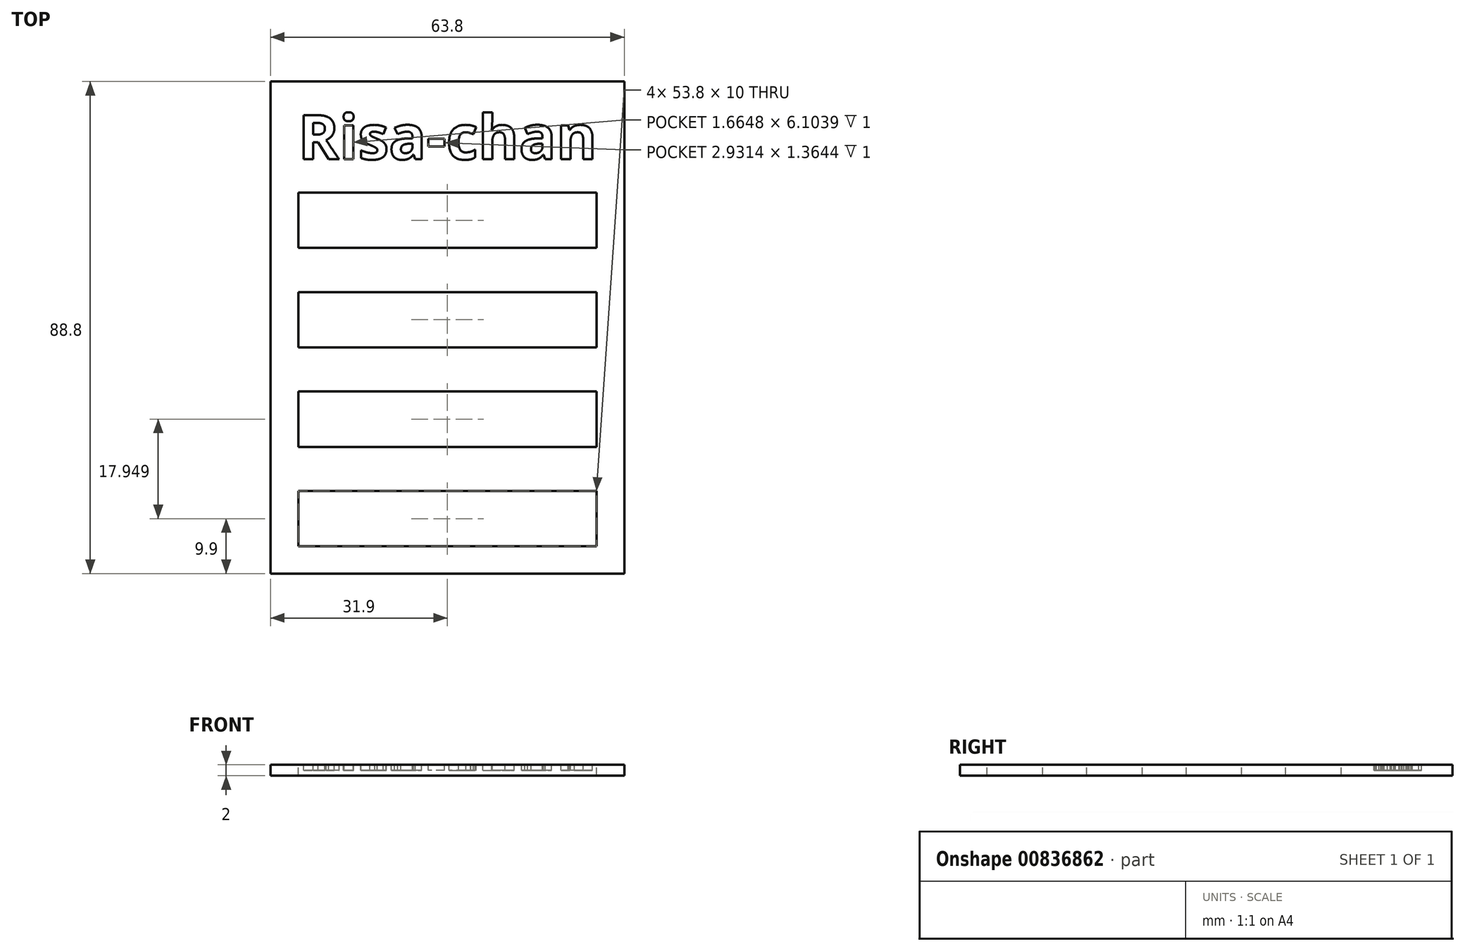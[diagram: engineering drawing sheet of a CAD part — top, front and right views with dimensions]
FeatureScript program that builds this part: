
annotation { "Feature Type Name" : "Feature", "Feature Type Description" : "" }
export const myFeature = defineFeature(function(context is Context, id is Id, definition is map)
    precondition{}
    {
        {
            var Q0;
            Q0=qCreatedBy(makeId("Top.planeOp"),FACE);
            var sketch = newSketch(context, id + "F0", { "sketchPlane" : qUnion([Q0])});
            skLineSegment(sketch, "E0.bottom", {"start": v(32, -44.5) * mm, "end": v(-32, -44.5) * mm});
            skLineSegment(sketch, "E0.top", {"start": v(32, 44.5) * mm, "end": v(-32, 44.5) * mm});
            skLineSegment(sketch, "E0.left", {"start": v(32, -44.5) * mm, "end": v(32, 44.5) * mm});
            skLineSegment(sketch, "E0.right", {"start": v(-32, -44.5) * mm, "end": v(-32, 44.5) * mm});
            skLineSegment(sketch, "E1.0", {"start": v(31.9, 44.4) * mm, "end": v(-31.9, 44.4) * mm});
            skLineSegment(sketch, "E1.1", {"start": v(31.9, -44.4) * mm, "end": v(31.9, 44.4) * mm});
            skLineSegment(sketch, "E1.2", {"start": v(31.9, -44.4) * mm, "end": v(-31.9, -44.4) * mm});
            skLineSegment(sketch, "E1.3", {"start": v(-31.9, -44.4) * mm, "end": v(-31.9, 44.4) * mm});
            skSolve(sketch);
        }
        {
            var Q0;
            Q0=makeQuery(id+"F0.imprint","IMPRINT",FACE,{"disambiguationData":[TD([[makeQuery(id+"F0.imprint","IMPRINT",EDGE,{"derivedFrom":sQuery(id+"F0.wireOp",EDGE,"E1.0")}),1.0]])]});
            extrude(context, id + "F1", {"entities" : qUnion([Q0]), "depth" : 2 * mm, "offsetDistance" : 25 * mm});
        }
        {
            var Q0;
            Q0=makeQuery(id+"F1.opExtrude","CAP_FACE",FACE,{"disambiguationData":[OSD([sQuery(id+"F0.wireOp",EDGE,"E1.0"),sQuery(id+"F0.wireOp",EDGE,"E1.1"),sQuery(id+"F0.wireOp",EDGE,"E1.2"),sQuery(id+"F0.wireOp",EDGE,"E1.3")])],"isStart":false});
            var sketch = newSketch(context, id + "F2", { "sketchPlane" : qUnion([Q0])});
            skText(sketch, "E2", { "text": "Risa-chan", "fontName": "OpenSans-Bold.ttf"});
            const initialGuessF2  = {"E2": [-0.0269, 0.03035, 1, 0, 0.00805]};
            skSetInitialGuess(sketch, initialGuessF2);
            skSolve(sketch);
        }
        {
            var Q0;
            Q0=qSketchRegion(id+"F2",true);
            extrude(context, id + "F3", {"entities" : qUnion([Q0]), "operationType" : NewBodyOperationType.REMOVE, "oppositeDirection" : true, "depth" : 1 * mm, "offsetDistance" : 25 * mm});
        }
        {
            var Q0;
            {var subQ0=sQuery(id+"F0.wireOp",EDGE,"E1.1");var subQ1=sQuery(id+"F0.wireOp",EDGE,"E1.3");var subQ2=sQuery(id+"F0.wireOp",EDGE,"E1.0");var subQ3=sQuery(id+"F0.wireOp",EDGE,"E1.2");Q0=makeQuery(id+"F3.boolean.opBoolean","SPLIT",FACE,{"disambiguationData":[TD([makeQuery(id+"F1.opExtrude","SWEPT_FACE",FACE,{"disambiguationData":[OSD([subQ2])]})])],"derivedFrom":makeQuery(id+"F1.opExtrude","CAP_FACE",FACE,{"disambiguationData":[OSD([subQ2,subQ0,subQ3,subQ1])],"isStart":false})});}
            var sketch = newSketch(context, id + "F4", { "sketchPlane" : qUnion([Q0])});
            skLineSegment(sketch, "E3.bottom", {"start": v(-26.9, 24.35) * mm, "end": v(26.9, 24.35) * mm});
            skLineSegment(sketch, "E3.top", {"start": v(-26.9, 14.35) * mm, "end": v(26.9, 14.35) * mm});
            skLineSegment(sketch, "E3.left", {"start": v(-26.9, 24.35) * mm, "end": v(-26.9, 14.35) * mm});
            skLineSegment(sketch, "E3.right", {"start": v(26.9, 24.35) * mm, "end": v(26.9, 14.35) * mm});
            skLineSegment(sketch, "E4.0.1.0", {"start": v(-26.9, -3.6) * mm, "end": v(26.9, -3.6) * mm});
            skLineSegment(sketch, "E4.0.1.1", {"start": v(26.9, 6.4) * mm, "end": v(26.9, -3.6) * mm});
            skLineSegment(sketch, "E4.0.1.2", {"start": v(-26.9, 6.4) * mm, "end": v(-26.9, -3.6) * mm});
            skLineSegment(sketch, "E4.0.1.3", {"start": v(-26.9, 6.4) * mm, "end": v(26.9, 6.4) * mm});
            skLineSegment(sketch, "E4.0.2.0", {"start": v(-26.9, -21.55) * mm, "end": v(26.9, -21.55) * mm});
            skLineSegment(sketch, "E4.0.2.1", {"start": v(26.9, -11.55) * mm, "end": v(26.9, -21.55) * mm});
            skLineSegment(sketch, "E4.0.2.2", {"start": v(-26.9, -11.55) * mm, "end": v(-26.9, -21.55) * mm});
            skLineSegment(sketch, "E4.0.2.3", {"start": v(-26.9, -11.55) * mm, "end": v(26.9, -11.55) * mm});
            skLineSegment(sketch, "E4.0.3.0", {"start": v(-26.9, -39.5) * mm, "end": v(26.9, -39.5) * mm});
            skLineSegment(sketch, "E4.0.3.1", {"start": v(26.9, -29.5) * mm, "end": v(26.9, -39.5) * mm});
            skLineSegment(sketch, "E4.0.3.2", {"start": v(-26.9, -29.5) * mm, "end": v(-26.9, -39.5) * mm});
            skLineSegment(sketch, "E4.0.3.3", {"start": v(-26.9, -29.5) * mm, "end": v(26.9, -29.5) * mm});
            skLineSegment(sketch, "E4.direction1", {"start": v(-26.9, 14.35) * mm, "end": v(-1.9, 14.35) * mm, "construction": true});
            skLineSegment(sketch, "E4.direction2", {"start": v(-26.9, 14.35) * mm, "end": v(-26.9, -3.6) * mm, "construction": true});
            skSolve(sketch);
        }
        {
            var Q0;
            Q0=qSketchRegion(id+"F4",true);
            extrude(context, id + "F5", {"entities" : qUnion([Q0]), "operationType" : NewBodyOperationType.REMOVE, "oppositeDirection" : true, "depth" : 25 * mm, "offsetDistance" : 25 * mm});
        }
    });
